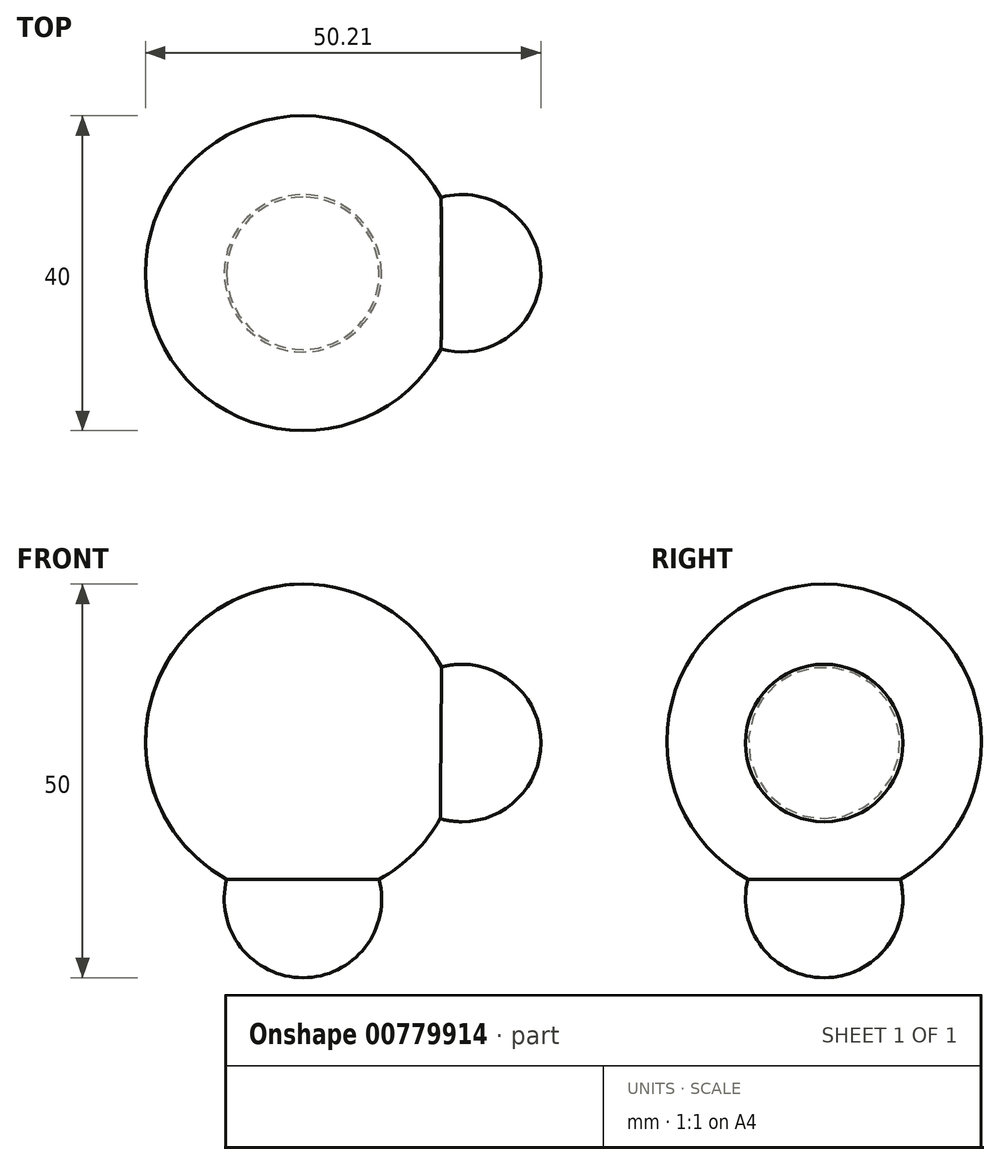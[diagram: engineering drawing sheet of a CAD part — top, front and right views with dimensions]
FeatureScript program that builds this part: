
annotation { "Feature Type Name" : "Feature", "Feature Type Description" : "" }
export const myFeature = defineFeature(function(context is Context, id is Id, definition is map)
    precondition{}
    {
        {
            var Q0;
            Q0=qCreatedBy(makeId("Front.planeOp"),FACE);
            var sketch = newSketch(context, id + "F0", { "sketchPlane" : qUnion([Q0])});
            skLineSegment(sketch, "E0", {"start": v(0, 40) * mm, "end": v(0, 0) * mm});
            skArc(sketch, "E1", {"start": v(0, 0) * mm, "mid": v(20, 20) * mm, "end": v(0, 40) * mm});
            skSolve(sketch);
        }
        {
            var Q0;
            Q0=qCreatedBy(makeId("Front.planeOp"),FACE);
            var sketch = newSketch(context, id + "F1", { "sketchPlane" : qUnion([Q0])});
            skLineSegment(sketch, "E2", {"start": v(0, 39.64) * mm, "end": v(0, 0) * mm, "construction": true});
            skLineSegment(sketch, "E3", {"start": v(0, 19.82) * mm, "end": v(20.21, 19.82) * mm, "construction": true});
            skSolve(sketch);
        }
        {
            var Q0;
            Q0 = qSketchRegion(id + "F0", true);
            var Q1;
            Q1=sQuery(id+"F0.wireOp",EDGE,"E0");
            revolve(context, id + "F2", {"surfaceOperationType" : NewSurfaceOperationType.NEW, "entities" : qUnion([Q0]), "axis" : qUnion([Q1]), "revolveType" : RevolveType.FULL});
        }
        {
            var Q0;
            Q0=qCreatedBy(makeId("Right.planeOp"),FACE);
            var sketch = newSketch(context, id + "F3", { "sketchPlane" : qUnion([Q0])});
            skLineSegment(sketch, "E4", {"start": v(0, 10) * mm, "end": v(0, -10) * mm});
            skArc(sketch, "E5", {"start": v(0, 10) * mm, "mid": v(-10, 0) * mm, "end": v(0, -10) * mm});
            skSolve(sketch);
        }
        {
            var Q0;
            Q0=makeQuery(id+"F3.imprint","IMPRINT",FACE,{"disambiguationData":[TD([[makeQuery(id+"F3.imprint","IMPRINT",EDGE,{"derivedFrom":sQuery(id+"F3.wireOp",EDGE,"E4")}),-1.0]])]});
            var Q1;
            Q1=sQuery(id+"F3.wireOp",EDGE,"E4");
            revolve(context, id + "F4", {"operationType" : NewBodyOperationType.ADD, "surfaceOperationType" : NewSurfaceOperationType.NEW, "entities" : qUnion([Q0]), "axis" : qUnion([Q1]), "revolveType" : RevolveType.FULL});
        }
        {
            var Q0;
            Q0=qCreatedBy(makeId("Front.planeOp"),FACE);
            var sketch = newSketch(context, id + "F5", { "sketchPlane" : qUnion([Q0])});
            skLineSegment(sketch, "E6", {"start": v(20.21, 29.82) * mm, "end": v(20.21, 9.82) * mm});
            skArc(sketch, "E7", {"start": v(20.21, 29.82) * mm, "mid": v(10.21, 19.82) * mm, "end": v(20.21, 9.82) * mm});
            skSolve(sketch);
        }
        {
            var Q0;
            Q0 = qSketchRegion(id + "F5", true);
            var Q1;
            Q1=sQuery(id+"F5.wireOp",EDGE,"E6");
            revolve(context, id + "F6", {"operationType" : NewBodyOperationType.ADD, "surfaceOperationType" : NewSurfaceOperationType.NEW, "entities" : qUnion([Q0]), "axis" : qUnion([Q1]), "revolveType" : RevolveType.FULL});
        }
    });
